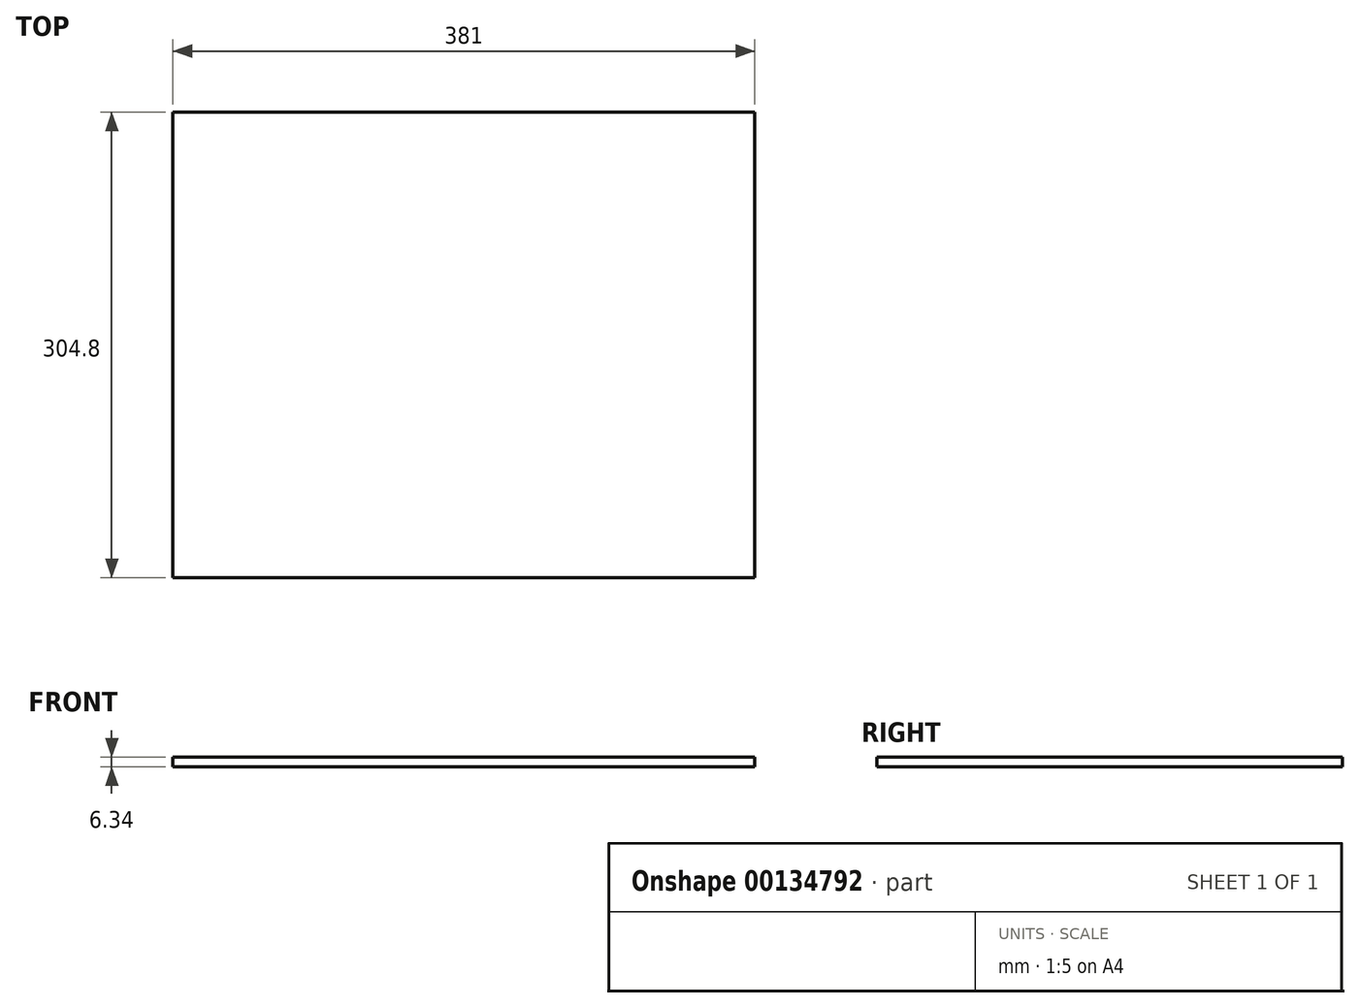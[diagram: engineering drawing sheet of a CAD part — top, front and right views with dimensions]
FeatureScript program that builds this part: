
annotation { "Feature Type Name" : "Feature", "Feature Type Description" : "" }
export const myFeature = defineFeature(function(context is Context, id is Id, definition is map)
    precondition{}
    {
        {
            var Q0;
            Q0=qCreatedBy(makeId("Top.planeOp"),FACE);
            var sketch = newSketch(context, id + "F0", { "sketchPlane" : qUnion([Q0])});
            skLineSegment(sketch, "E0.bottom", {"start": v(190.5, 152.4) * mm, "end": v(-190.5, 152.4) * mm});
            skLineSegment(sketch, "E0.top", {"start": v(190.5, -152.4) * mm, "end": v(-190.5, -152.4) * mm});
            skLineSegment(sketch, "E0.left", {"start": v(190.5, 152.4) * mm, "end": v(190.5, -152.4) * mm});
            skLineSegment(sketch, "E0.right", {"start": v(-190.5, 152.4) * mm, "end": v(-190.5, -152.4) * mm});
            skPoint(sketch, "E0.middle", {"position": v(0, 0) * mm});
            skSolve(sketch);
        }
        {
            var Q0;
            Q0=makeQuery(id+"F0.imprint","IMPRINT",FACE,{"disambiguationData":[TD([[makeQuery(id+"F0.imprint","IMPRINT",EDGE,{"derivedFrom":sQuery(id+"F0.wireOp",EDGE,"E0.bottom")}),1.0]])]});
            extrude(context, id + "F1", {"entities" : qUnion([Q0]), "depth" : 6.35 * mm, "symmetric" : true});
        }
    });
